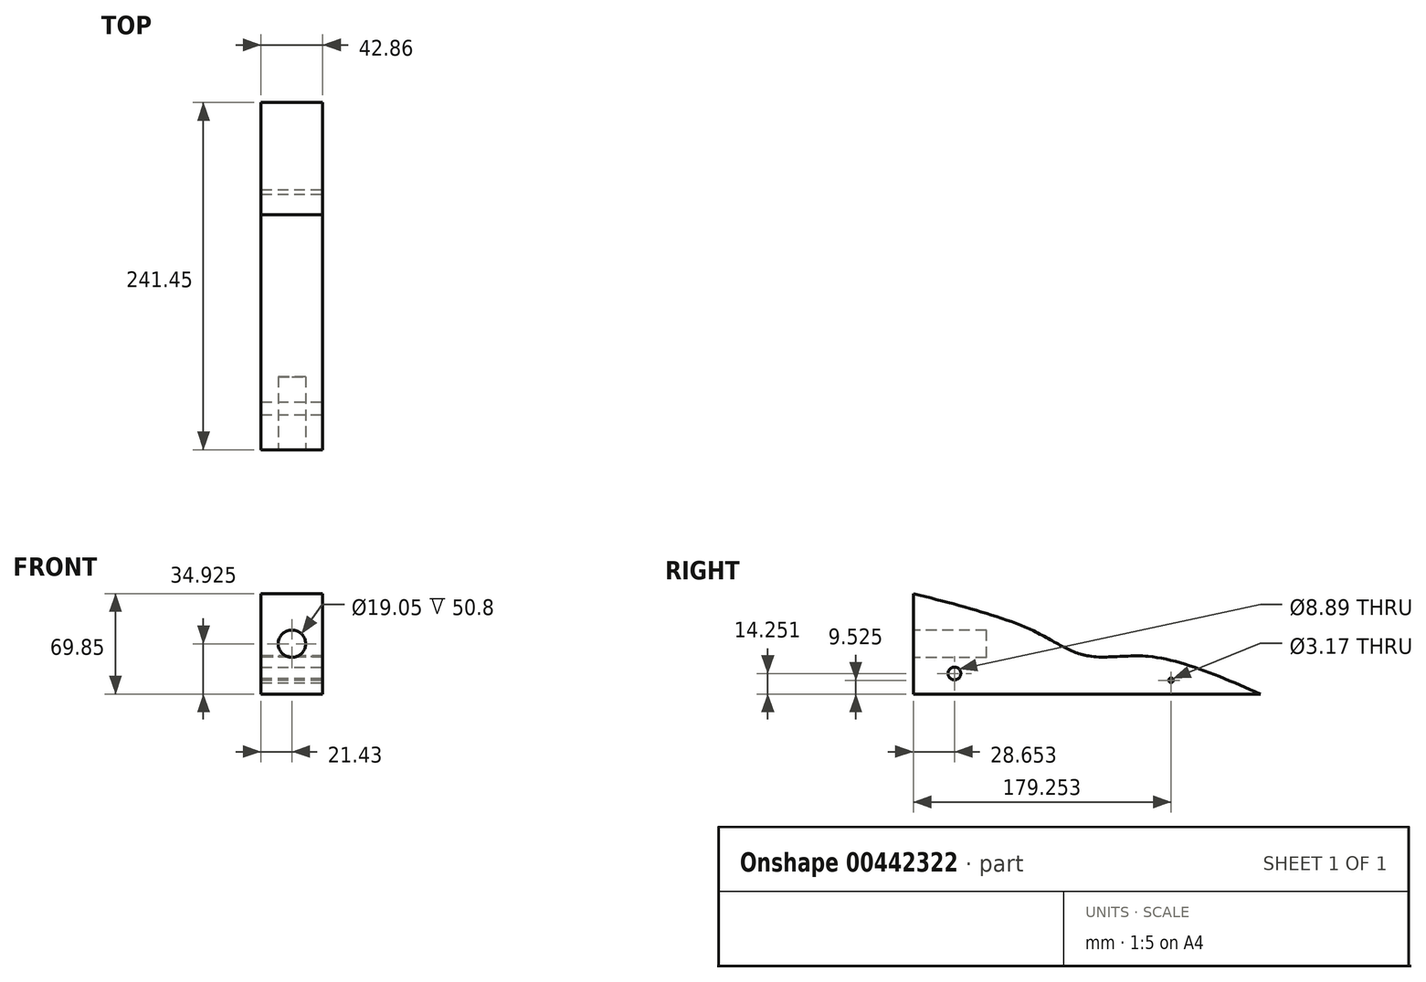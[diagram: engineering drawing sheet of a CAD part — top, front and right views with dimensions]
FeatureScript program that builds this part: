
annotation { "Feature Type Name" : "Feature", "Feature Type Description" : "" }
export const myFeature = defineFeature(function(context is Context, id is Id, definition is map)
    precondition{}
    {
        {
            var Q0;
            Q0=qCreatedBy(makeId("Right.planeOp"),FACE);
            var sketch = newSketch(context, id + "F0", { "sketchPlane" : qUnion([Q0])});
            skLineSegment(sketch, "E0", {"start": v(-152.4, 0) * mm, "end": v(152.4, 0) * mm});
            skLineSegment(sketch, "E1", {"start": v(-152.4, 0) * mm, "end": v(-152.4, 69.85) * mm});
            skLineSegment(sketch, "E2", {"start": v(152.4, 0) * mm, "end": v(152.4, 19.05) * mm});
            skLineSegment(sketch, "E3", {"start": v(152.4, 19.05) * mm, "end": v(-152.4, 69.85) * mm});
            skPoint(sketch, "E4.endSnap0", {"position": v(-152.4, 34.93) * mm});
            skLineSegment(sketch, "E5.0", {"start": v(-95.25, 50.8) * mm, "end": v(-152.4, 50.8) * mm, "construction": true});
            skLineSegment(sketch, "E5.1", {"start": v(-95.25, 50.8) * mm, "end": v(-95.25, 19.05) * mm, "construction": true});
            skLineSegment(sketch, "E5.2", {"start": v(-95.25, 19.05) * mm, "end": v(-152.4, 19.05) * mm, "construction": true});
            skSolve(sketch);
        }
        {
            var Q0;
            Q0=makeQuery(id+"F0.imprint","IMPRINT",FACE,{"disambiguationData":[TD([[makeQuery(id+"F0.imprint","IMPRINT",EDGE,{"derivedFrom":sQuery(id+"F0.wireOp",EDGE,"E0")}),1.0]])]});
            extrude(context, id + "F1", {"entities" : qUnion([Q0]), "depth" : 42.86 * mm, "symmetric" : true});
        }
        {
            var Q0;
            Q0=makeQuery(id+"F1.opExtrude","SWEPT_FACE",FACE,{"disambiguationData":[OSD([sQuery(id+"F0.wireOp",EDGE,"E1")])]});
            var sketch = newSketch(context, id + "F2", { "sketchPlane" : qUnion([Q0])});
            skLineSegment(sketch, "E6", {"start": v(21.43, 34.93) * mm, "end": v(0, 34.93) * mm, "construction": true});
            skCircle(sketch, "E7", {"center": v(0, 34.93) * mm, "radius": 9.53 * mm});
            skSolve(sketch);
        }
        {
            var Q0;
            Q0=makeQuery(id+"F2.imprint","IMPRINT",FACE,{"disambiguationData":[TD([[makeQuery(id+"F2.imprint","IMPRINT",EDGE,{"derivedFrom":sQuery(id+"F2.wireOp",EDGE,"E7")}),1.0]])]});
            var Q1;
            Q1=sQuery(id+"F2.wireOp",EDGE,"E7");
            extrude(context, id + "F3", {"entities" : qUnion([Q0]), "operationType" : NewBodyOperationType.REMOVE, "surfaceEntities" : qUnion([Q1]), "oppositeDirection" : true, "depth" : 50.8 * mm});
        }
        {
            var Q0;
            Q0=makeQuery(id+"F1.opExtrude","CAP_FACE",FACE,{"disambiguationData":[OSD([sQuery(id+"F0.wireOp",EDGE,"E0"),sQuery(id+"F0.wireOp",EDGE,"E1"),sQuery(id+"F0.wireOp",EDGE,"E2"),sQuery(id+"F0.wireOp",EDGE,"E3")])],"isStart":false});
            var sketch = newSketch(context, id + "F4", { "sketchPlane" : qUnion([Q0])});
            skLineSegment(sketch, "E8", {"start": v(-152.4, 34.93) * mm, "end": v(-152.4, 44.45) * mm, "construction": true});
            skLineSegment(sketch, "E9.0", {"start": v(-95.25, 19.05) * mm, "end": v(-152.4, 19.05) * mm, "construction": true});
            skLineSegment(sketch, "E9.1", {"start": v(-95.25, 50.8) * mm, "end": v(-95.25, 19.05) * mm, "construction": true});
            skLineSegment(sketch, "E9.2", {"start": v(-152.4, 50.8) * mm, "end": v(-95.25, 50.8) * mm, "construction": true});
            skLineSegment(sketch, "E10", {"start": v(57.15, 0) * mm, "end": v(57.15, 34.93) * mm, "construction": true});
            skLineSegment(sketch, "E11", {"start": v(-152.4, 44.45) * mm, "end": v(-101.6, 44.45) * mm, "construction": true});
            skLineSegment(sketch, "E12", {"start": v(-101.6, 44.45) * mm, "end": v(-101.6, 25.4) * mm, "construction": true});
            skLineSegment(sketch, "E13", {"start": v(-101.6, 25.4) * mm, "end": v(-152.4, 25.4) * mm, "construction": true});
            skFitSpline(sketch, "E14", {"points": [v(-152.4, 69.85) * mm, v(-68.84, 43.9) * mm, v(-32, 26.68) * mm, v(11.06, 26.2) * mm, v(89.05, 0) * mm], "startDerivative": vector(312.17, -79.46) * mm, "endDerivative": vector(285.62, -124.47) * mm});
            skLineSegment(sketch, "E15", {"start": v(-152.4, 69.85) * mm, "end": v(-152.4, 0) * mm});
            skLineSegment(sketch, "E16", {"start": v(-152.4, 0) * mm, "end": v(89.05, 0) * mm});
            skFitSpline(sketch, "E17", {"points": [v(-152.4, 69.85) * mm, v(-121.37, 61.95) * mm, v(-68.84, 43.9) * mm, v(-32, 26.68) * mm, v(11.06, 26.2) * mm, v(61.51, 12) * mm, v(89.05, 0) * mm], "startDerivative": vector(194.68, -47.64) * mm, "endDerivative": vector(176.94, -80.34) * mm});
            skCircle(sketch, "E18", {"center": v(26.85, 9.53) * mm, "radius": 1.59 * mm});
            skCircle(sketch, "E19", {"center": v(-123.75, 14.25) * mm, "radius": 4.45 * mm});
            skSolve(sketch);
        }
        {
            var Q0;
            {var subQ6=sQuery(id+"F4.wireOp",EDGE,"E15");Q0=makeQuery(id+"F4.imprint","IMPRINT",FACE,{"disambiguationData":[TD([[makeQuery(id+"F4.imprint","IMPRINT",EDGE,{"derivedFrom":subQ6}),-1.0]])]});}
            extrude(context, id + "F5", {"entities" : qUnion([Q0]), "operationType" : NewBodyOperationType.INTERSECT, "endBound" : BoundingType.THROUGH_ALL, "oppositeDirection" : true, "depth" : 25.4 * mm});
        }
    });
